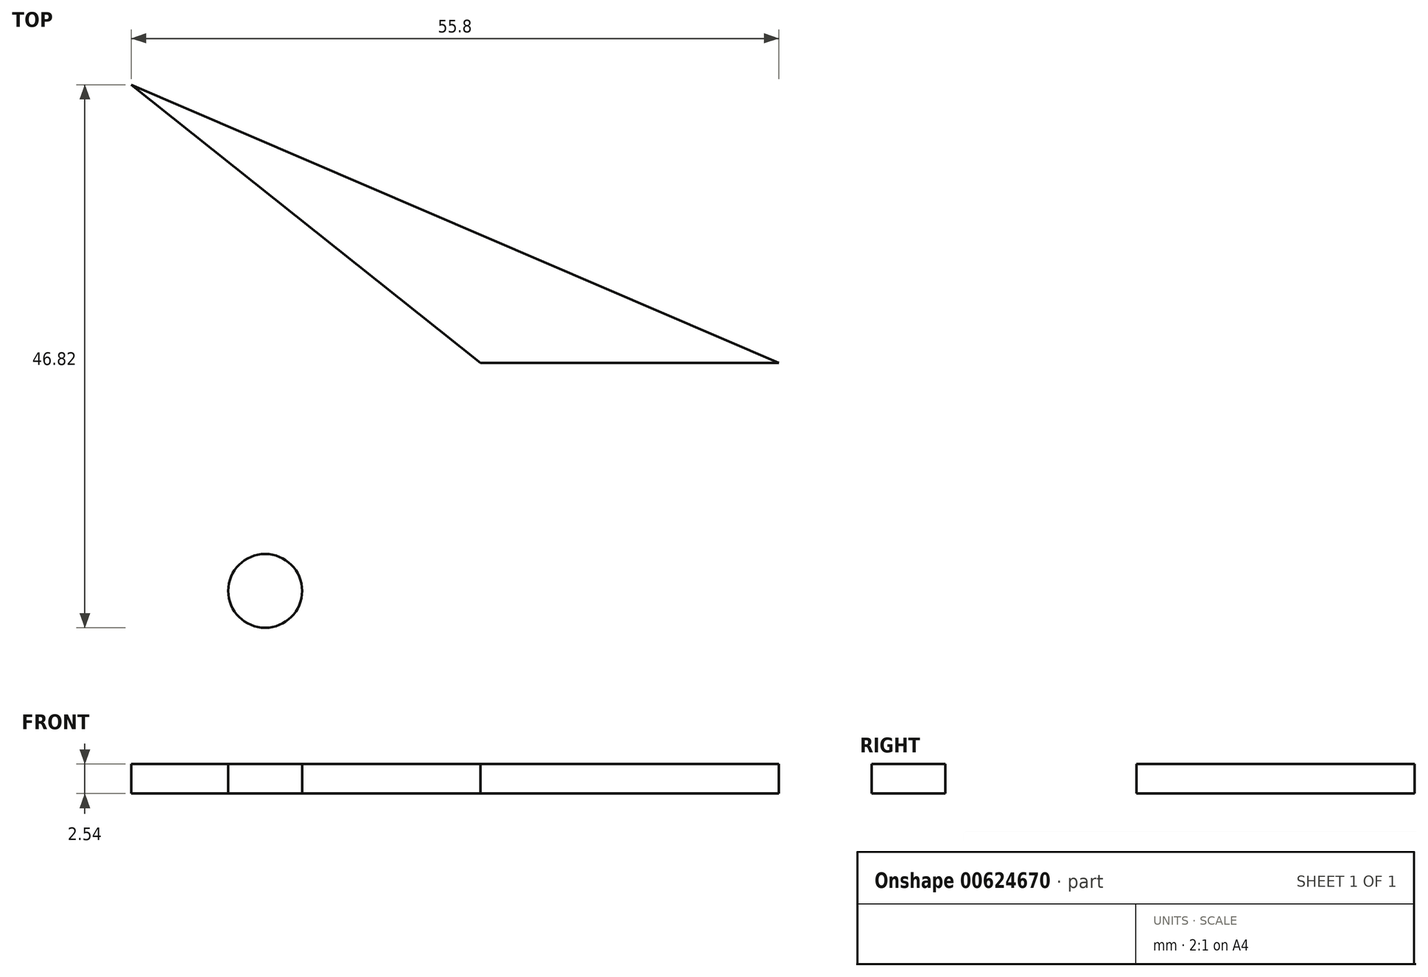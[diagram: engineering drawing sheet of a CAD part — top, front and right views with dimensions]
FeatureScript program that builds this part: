
annotation { "Feature Type Name" : "Feature", "Feature Type Description" : "" }
export const myFeature = defineFeature(function(context is Context, id is Id, definition is map)
    precondition{}
    {
        {
            var Q0;
            Q0=qCreatedBy(makeId("Top.planeOp"),FACE);
            var sketch = newSketch(context, id + "F0", { "sketchPlane" : qUnion([Q0])});
            skLineSegment(sketch, "E0", {"start": v(-64.34, 56.74) * mm, "end": v(-34.25, 32.76) * mm});
            skLineSegment(sketch, "E1", {"start": v(-34.25, 32.76) * mm, "end": v(-8.54, 32.76) * mm});
            skLineSegment(sketch, "E2.bottom", {"start": v(-59.64, 18.8) * mm, "end": v(-40.83, 18.8) * mm});
            skLineSegment(sketch, "E2.top", {"start": v(-59.64, -1.57) * mm, "end": v(-40.83, -1.57) * mm});
            skLineSegment(sketch, "E2.left", {"start": v(-59.64, 18.8) * mm, "end": v(-59.64, -1.57) * mm});
            skLineSegment(sketch, "E2.right", {"start": v(-40.83, 18.8) * mm, "end": v(-40.83, -1.57) * mm});
            skLineSegment(sketch, "E3", {"start": v(-64.34, 56.74) * mm, "end": v(-8.54, 32.76) * mm});
            skSolve(sketch);
        }
        {
            var Q0;
            Q0 = qSketchRegion(id + "F0", true);
            extrude(context, id + "F1", {"entities" : qUnion([Q0]), "depth" : 2.54 * mm, "offsetDistance" : 25.4 * mm});
        }
        {
            var Q0;
            Q0=makeQuery(id+"F1.opExtrude","CAP_FACE",FACE,{"disambiguationData":[OSD([sQuery(id+"F0.wireOp",EDGE,"E2.bottom"),sQuery(id+"F0.wireOp",EDGE,"E2.top"),sQuery(id+"F0.wireOp",EDGE,"E2.left"),sQuery(id+"F0.wireOp",EDGE,"E2.right")])],"isStart":false});
            var sketch = newSketch(context, id + "F2", { "sketchPlane" : qUnion([Q0])});
            skCircle(sketch, "E4", {"center": v(-52.8, 13.1) * mm, "radius": 3.18 * mm});
            skSolve(sketch);
        }
        {
            var Q0;
            Q0=makeQuery(id+"F2.imprint","IMPRINT",FACE,{"disambiguationData":[TD([[makeQuery(id+"F2.imprint","IMPRINT",EDGE,{"derivedFrom":sQuery(id+"F2.wireOp",EDGE,"E4")}),-1.0]])]});
            extrude(context, id + "F3", {"entities" : qUnion([Q0]), "operationType" : NewBodyOperationType.REMOVE, "oppositeDirection" : true, "depth" : 25.4 * mm, "offsetDistance" : 25.4 * mm});
        }
    });
